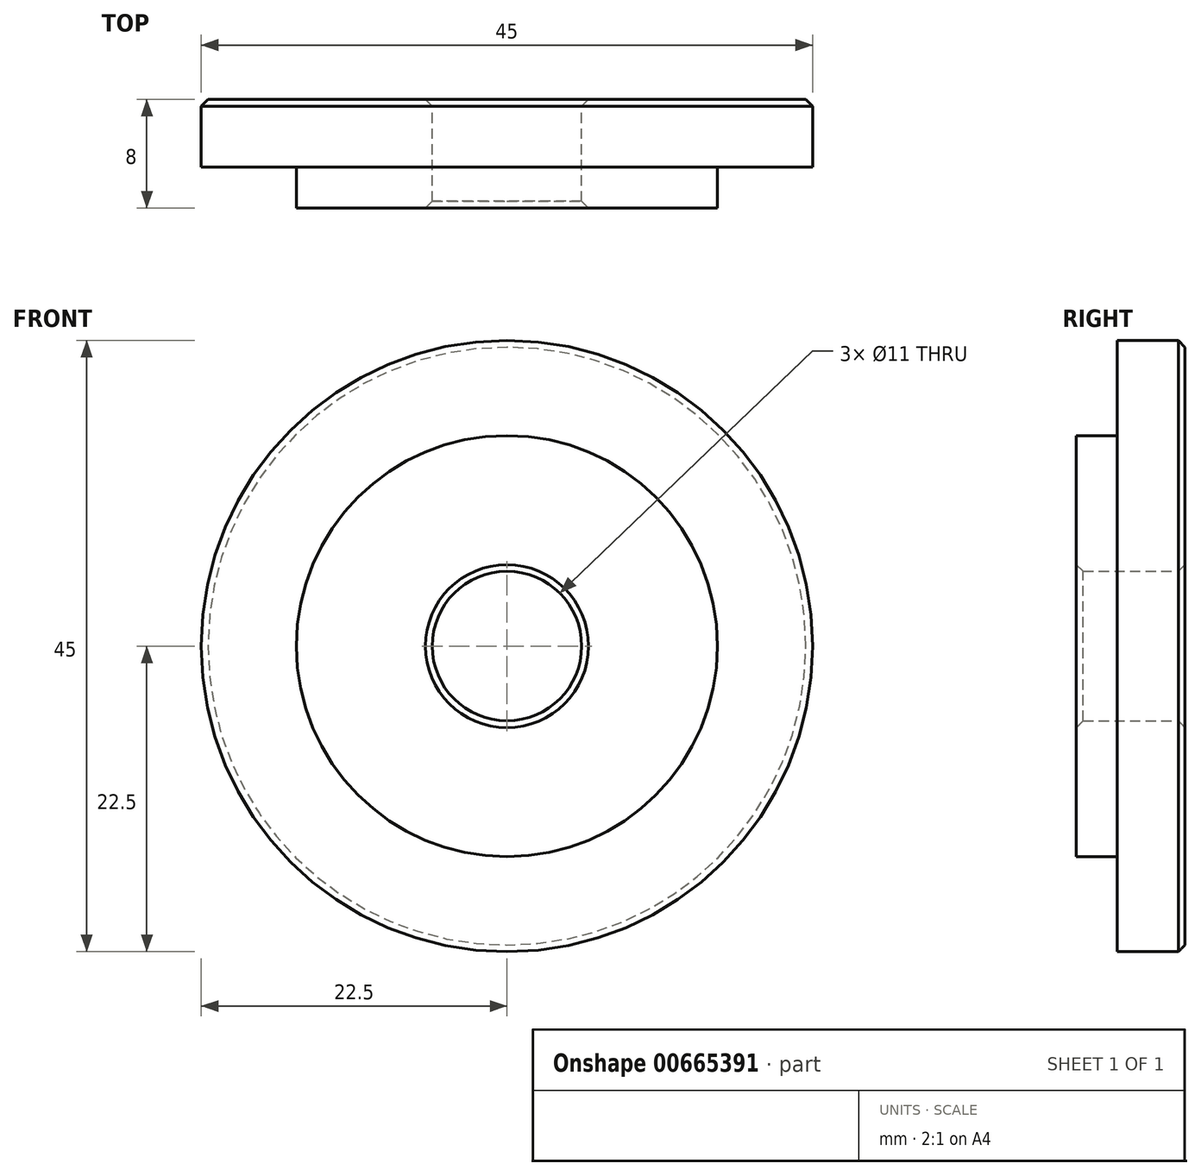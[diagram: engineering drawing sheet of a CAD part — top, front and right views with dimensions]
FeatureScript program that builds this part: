
annotation { "Feature Type Name" : "Feature", "Feature Type Description" : "" }
export const myFeature = defineFeature(function(context is Context, id is Id, definition is map)
    precondition{}
    {
        {
            var Q0;
            Q0=qCreatedBy(makeId("Front.planeOp"),FACE);
            var sketch = newSketch(context, id + "F0", { "sketchPlane" : qUnion([Q0])});
            skCircle(sketch, "E0", {"center": v(0, 0) * mm, "radius": 22.5 * mm});
            skCircle(sketch, "E1", {"center": v(0, 0) * mm, "radius": 5.5 * mm});
            skSolve(sketch);
        }
        {
            var Q0;
            Q0 = qSketchRegion(id + "F0", true);
            extrude(context, id + "F1", {"entities" : qUnion([Q0]), "depth" : 8 * mm, "offsetDistance" : 25 * mm});
        }
        {
            var Q0;
            Q0=makeQuery(id+"F1.opExtrude","CAP_FACE",FACE,{"disambiguationData":[OSD([sQuery(id+"F0.wireOp",EDGE,"E0"),sQuery(id+"F0.wireOp",EDGE,"E1")])],"isStart":false});
            var sketch = newSketch(context, id + "F2", { "sketchPlane" : qUnion([Q0])});
            skCircle(sketch, "E2", {"center": v(0, 0) * mm, "radius": 15.5 * mm});
            skSolve(sketch);
        }
        {
            var Q0;
            Q0=makeQuery(id+"F2.imprint","IMPRINT",FACE,{"disambiguationData":[TD([[makeQuery(id+"F2.imprint","IMPRINT",EDGE,{"derivedFrom":sQuery(id+"F2.wireOp",EDGE,"E2")}),-1.0]])]});
            extrude(context, id + "F3", {"entities" : qUnion([Q0]), "operationType" : NewBodyOperationType.REMOVE, "oppositeDirection" : true, "depth" : 3 * mm, "offsetDistance" : 25 * mm});
        }
        {
            var Q0;
            Q0=makeQuery(id+"F1.opExtrude","CAP_EDGE",EDGE,{"disambiguationData":[OSD([sQuery(id+"F0.wireOp",EDGE,"E0")])],"isStart":true});
            var Q1;
            Q1=makeQuery(id+"F3.boolean.opBoolean","COPY",EDGE,{"derivedFrom":makeQuery(id+"F3.opExtrude","CAP_EDGE",EDGE,{"disambiguationData":[OSD([sQuery(id+"F0.wireOp",EDGE,"E0")])],"isStart":false})});
            var Q2;
            Q2=makeQuery(id+"F3.boolean.opBoolean","COPY",EDGE,{"derivedFrom":makeQuery(id+"F3.opExtrude","CAP_EDGE",EDGE,{"disambiguationData":[OSD([sQuery(id+"F2.wireOp",EDGE,"E2")])],"isStart":true})});
            chamfer(context, id + "F4", {"entities" : qUnion([Q0, Q1, Q2]), "width" : .5 * mm, "tangentPropagation" : true});
        }
        {
            var Q0;
            Q0=makeQuery(id+"F1.opExtrude","CAP_EDGE",EDGE,{"disambiguationData":[OSD([sQuery(id+"F0.wireOp",EDGE,"E1")])],"isStart":false});
            var Q1;
            Q1=makeQuery(id+"F1.opExtrude","CAP_EDGE",EDGE,{"disambiguationData":[OSD([sQuery(id+"F0.wireOp",EDGE,"E1")])],"isStart":true});
            chamfer(context, id + "F5", {"entities" : qUnion([Q0, Q1]), "width" : .5 * mm, "tangentPropagation" : true});
        }
    });
